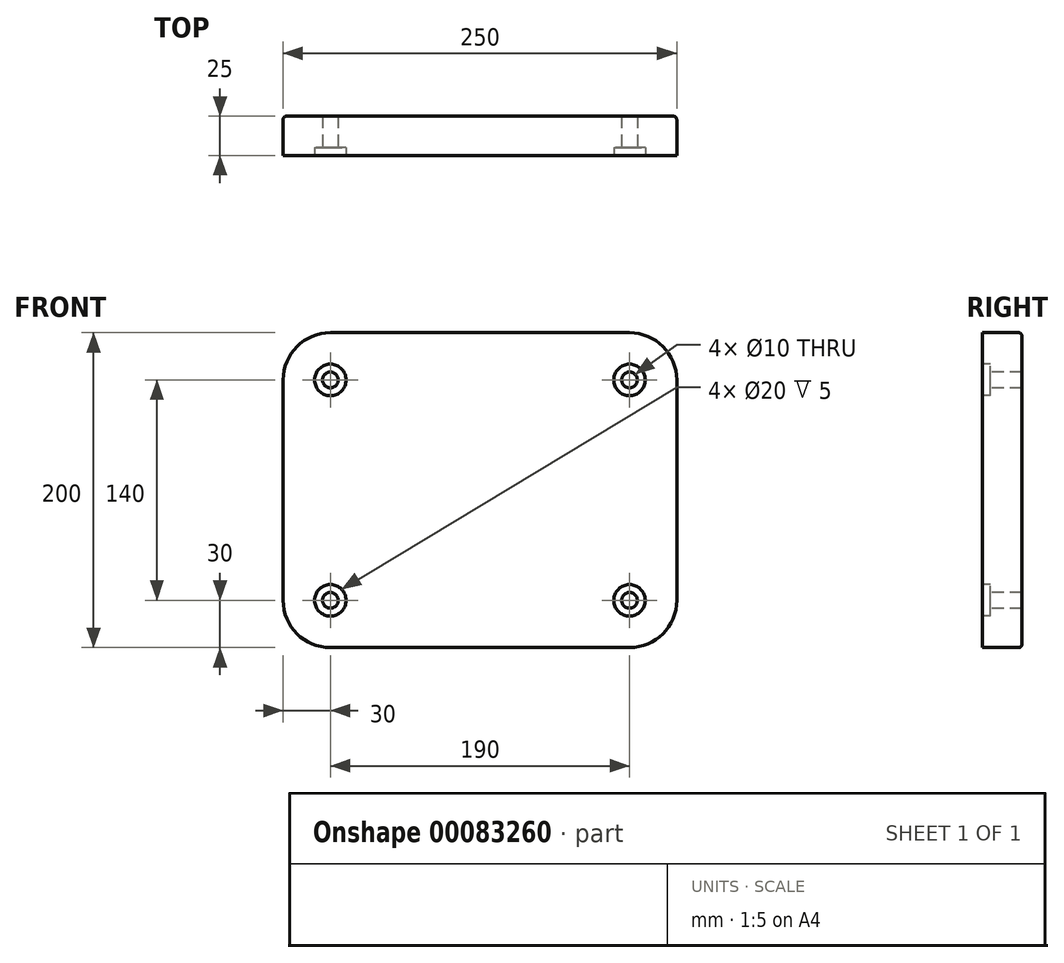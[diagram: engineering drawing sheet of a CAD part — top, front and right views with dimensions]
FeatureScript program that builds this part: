
annotation { "Feature Type Name" : "Feature", "Feature Type Description" : "" }
export const myFeature = defineFeature(function(context is Context, id is Id, definition is map)
    precondition{}
    {
        {
            var Q0;
            Q0=qCreatedBy(makeId("Front.planeOp"),FACE);
            var sketch = newSketch(context, id + "F0", { "sketchPlane" : qUnion([Q0])});
            skLineSegment(sketch, "E0.bottom", {"start": v(125, 100) * mm, "end": v(-125, 100) * mm});
            skLineSegment(sketch, "E0.top", {"start": v(125, -100) * mm, "end": v(-125, -100) * mm});
            skLineSegment(sketch, "E0.left", {"start": v(125, 100) * mm, "end": v(125, -100) * mm});
            skLineSegment(sketch, "E0.right", {"start": v(-125, 100) * mm, "end": v(-125, -100) * mm});
            skPoint(sketch, "E0.middle", {"position": v(0, 0) * mm});
            skSolve(sketch);
        }
        {
            var Q0;
            Q0=makeQuery(id+"F0.imprint","IMPRINT",FACE,{"disambiguationData":[TD([[makeQuery(id+"F0.imprint","IMPRINT",EDGE,{"derivedFrom":sQuery(id+"F0.wireOp",EDGE,"E0.bottom")}),1.0]])]});
            extrude(context, id + "F1", {"entities" : qUnion([Q0]), "depth" : 25 * mm});
        }
        {
            var Q0;
            Q0=makeQuery(id+"F1.opExtrude","SWEPT_EDGE",EDGE,{"disambiguationData":[OSD([sQuery(id+"F0.wireOp",EDGE,"E0.bottom"),sQuery(id+"F0.wireOp",EDGE,"E0.right")])]});
            var Q1;
            Q1=makeQuery(id+"F1.opExtrude","SWEPT_EDGE",EDGE,{"disambiguationData":[OSD([sQuery(id+"F0.wireOp",EDGE,"E0.top"),sQuery(id+"F0.wireOp",EDGE,"E0.right")])]});
            var Q2;
            Q2=makeQuery(id+"F1.opExtrude","SWEPT_EDGE",EDGE,{"disambiguationData":[OSD([sQuery(id+"F0.wireOp",EDGE,"E0.bottom"),sQuery(id+"F0.wireOp",EDGE,"E0.left")])]});
            var Q3;
            Q3=makeQuery(id+"F1.opExtrude","SWEPT_EDGE",EDGE,{"disambiguationData":[OSD([sQuery(id+"F0.wireOp",EDGE,"E0.top"),sQuery(id+"F0.wireOp",EDGE,"E0.left")])]});
            fillet(context, id + "F2", {"entities" : qUnion([Q0, Q1, Q2, Q3]), "radius" : 30 * mm, "tangentPropagation" : true, "allowEdgeOverflow" : false});
        }
        {
            var Q0;
            Q0=makeQuery(id+"F1.opExtrude","CAP_FACE",FACE,{"disambiguationData":[OSD([sQuery(id+"F0.wireOp",EDGE,"E0.bottom"),sQuery(id+"F0.wireOp",EDGE,"E0.top"),sQuery(id+"F0.wireOp",EDGE,"E0.left"),sQuery(id+"F0.wireOp",EDGE,"E0.right")])],"isStart":false});
            var sketch = newSketch(context, id + "F3", { "sketchPlane" : qUnion([Q0])});
            skPoint(sketch, "E1", {"position": v(-95, 70) * mm});
            skPoint(sketch, "E2", {"position": v(-95, -70) * mm});
            skPoint(sketch, "E3", {"position": v(95, -70) * mm});
            skPoint(sketch, "E4", {"position": v(95, 70) * mm});
            skSolve(sketch);
        }
        {
            var Q0;
            Q0=sQuery(id+"F3.wireOp",VERTEX,"E1");
            var Q1;
            Q1=sQuery(id+"F3.wireOp",VERTEX,"E2");
            var Q2;
            Q2=sQuery(id+"F3.wireOp",VERTEX,"E3");
            var Q3;
            Q3=sQuery(id+"F3.wireOp",VERTEX,"E4");
            var Q4;
            Q4=makeQuery(id+"F1.opExtrude","SWEPT_BODY",BODY,{"disambiguationData":[OSD([sQuery(id+"F0.wireOp",EDGE,"E0.bottom"),sQuery(id+"F0.wireOp",EDGE,"E0.top"),sQuery(id+"F0.wireOp",EDGE,"E0.left"),sQuery(id+"F0.wireOp",EDGE,"E0.right")])]});
            hole(context, id + "F4", {"style" : HoleStyle.C_BORE, "endStyle" : HoleEndStyle.THROUGH, "holeDiameter" : 10 * mm, "cBoreDiameter" : 20 * mm, "cBoreDepth" : 5 * mm, "locations" : qUnion([Q0, Q1, Q2, Q3]), "scope" : qUnion([Q4]), "isTappedThrough" : true});
        }
        {
            var Q0;
            Q0=makeQuery(id+"F1.opExtrude","CAP_EDGE",EDGE,{"disambiguationData":[OSD([sQuery(id+"F0.wireOp",EDGE,"E0.top")])],"isStart":true});
            fillet(context, id + "F5", {"entities" : qUnion([Q0]), "radius" : 2 * mm, "tangentPropagation" : true, "allowEdgeOverflow" : false});
        }
    });
